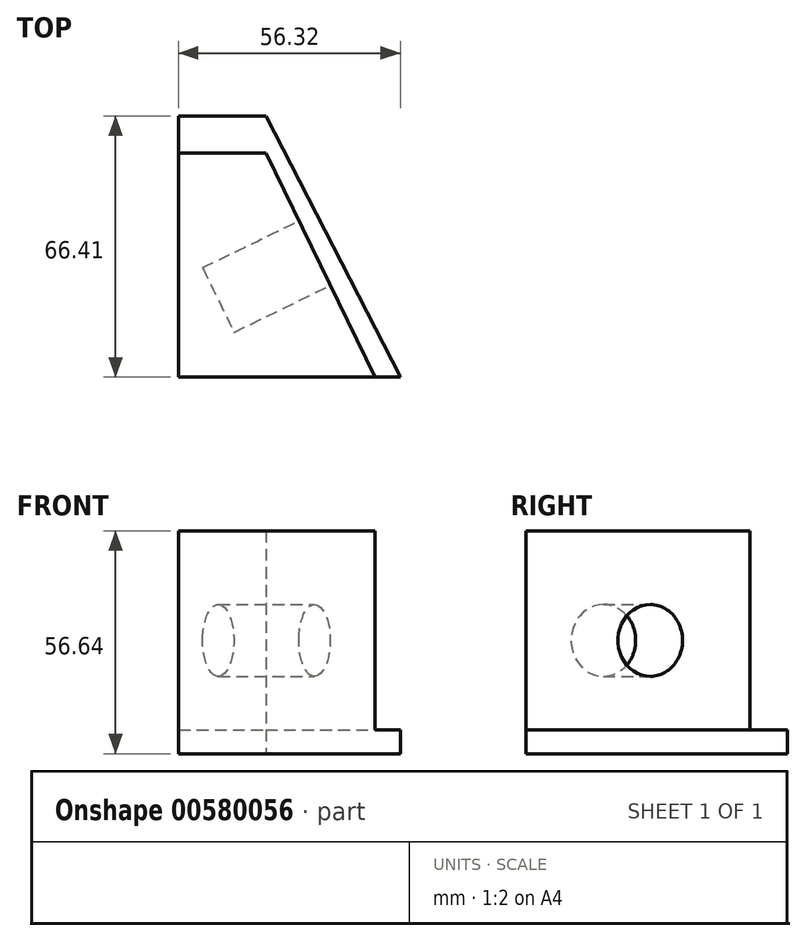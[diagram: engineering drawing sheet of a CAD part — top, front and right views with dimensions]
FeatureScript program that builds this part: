
annotation { "Feature Type Name" : "Feature", "Feature Type Description" : "" }
export const myFeature = defineFeature(function(context is Context, id is Id, definition is map)
    precondition{}
    {
        {
            var Q0;
            Q0=qCreatedBy(makeId("Top.planeOp"),FACE);
            var sketch = newSketch(context, id + "F0", { "sketchPlane" : qUnion([Q0])});
            skLineSegment(sketch, "E0.bottom", {"start": v(0, 0) * mm, "end": v(-22.17, 0) * mm});
            skLineSegment(sketch, "E0.top", {"start": v(0, 66.4) * mm, "end": v(-22.17, 66.4) * mm});
            skLineSegment(sketch, "E0.left", {"start": v(0, 0) * mm, "end": v(0, 66.4) * mm});
            skLineSegment(sketch, "E0.right", {"start": v(-22.17, 0) * mm, "end": v(-22.17, 66.4) * mm});
            skLineSegment(sketch, "E1", {"start": v(0, 66.4) * mm, "end": v(34.15, 0) * mm});
            skLineSegment(sketch, "E2", {"start": v(34.15, 0) * mm, "end": v(0, 0) * mm});
            skSolve(sketch);
        }
        {
            var Q0;
            Q0=makeQuery(id+"F0.imprint","IMPRINT",FACE,{"disambiguationData":[TD([[makeQuery(id+"F0.imprint","IMPRINT",EDGE,{"derivedFrom":sQuery(id+"F0.wireOp",EDGE,"E0.left")}),-1.0]])]});
            var Q1;
            Q1=makeQuery(id+"F0.imprint","IMPRINT",FACE,{"disambiguationData":[TD([[makeQuery(id+"F0.imprint","IMPRINT",EDGE,{"derivedFrom":sQuery(id+"F0.wireOp",EDGE,"E0.bottom")}),-1.0]])]});
            extrude(context, id + "F1", {"entities" : qUnion([Q0, Q1]), "depth" : 6.1 * mm, "offsetDistance" : 25.4 * mm});
        }
        {
            var Q0;
            Q0=makeQuery(id+"F1.opExtrude","CAP_FACE",FACE,{"disambiguationData":[OSD([sQuery(id+"F0.wireOp",EDGE,"E0.bottom"),sQuery(id+"F0.wireOp",EDGE,"E0.top"),sQuery(id+"F0.wireOp",EDGE,"E0.right"),sQuery(id+"F0.wireOp",EDGE,"E1"),sQuery(id+"F0.wireOp",EDGE,"E2")])],"isStart":false});
            var sketch = newSketch(context, id + "F2", { "sketchPlane" : qUnion([Q0])});
            skLineSegment(sketch, "E3", {"start": v(-22.17, 56.9) * mm, "end": v(0, 56.9) * mm});
            skLineSegment(sketch, "E4", {"start": v(0, 56.9) * mm, "end": v(27.68, 0) * mm});
            skLineSegment(sketch, "E5", {"start": v(-22.17, 56.9) * mm, "end": v(-22.17, 0) * mm});
            skLineSegment(sketch, "E6", {"start": v(-22.17, 0) * mm, "end": v(27.68, 0) * mm});
            skSolve(sketch);
        }
        {
            var Q0;
            Q0=makeQuery(id+"F2.imprint","IMPRINT",FACE,{"disambiguationData":[TD([[makeQuery(id+"F2.imprint","IMPRINT",EDGE,{"derivedFrom":sQuery(id+"F2.wireOp",EDGE,"E3")}),-1.0]])]});
            extrude(context, id + "F3", {"entities" : qUnion([Q0]), "operationType" : NewBodyOperationType.ADD, "depth" : 50.55 * mm, "offsetDistance" : 25.4 * mm});
        }
        {
            var Q0;
            Q0=makeQuery(id+"F3.opExtrude","SWEPT_FACE",FACE,{"disambiguationData":[OSD([sQuery(id+"F2.wireOp",EDGE,"E4")])]});
            var sketch = newSketch(context, id + "F4", { "sketchPlane" : qUnion([Q0])});
            skCircle(sketch, "E7", {"center": v(22.91, 28.78) * mm, "radius": 9.12 * mm});
            skSolve(sketch);
        }
        {
            var Q0;
            Q0=makeQuery(id+"F4.imprint","IMPRINT",FACE,{"disambiguationData":[TD([[makeQuery(id+"F4.imprint","IMPRINT",EDGE,{"derivedFrom":sQuery(id+"F4.wireOp",EDGE,"E7")}),1.0]])]});
            extrude(context, id + "F5", {"entities" : qUnion([Q0]), "operationType" : NewBodyOperationType.REMOVE, "oppositeDirection" : true, "depth" : 27.18 * mm, "offsetDistance" : 25.4 * mm});
        }
    });
